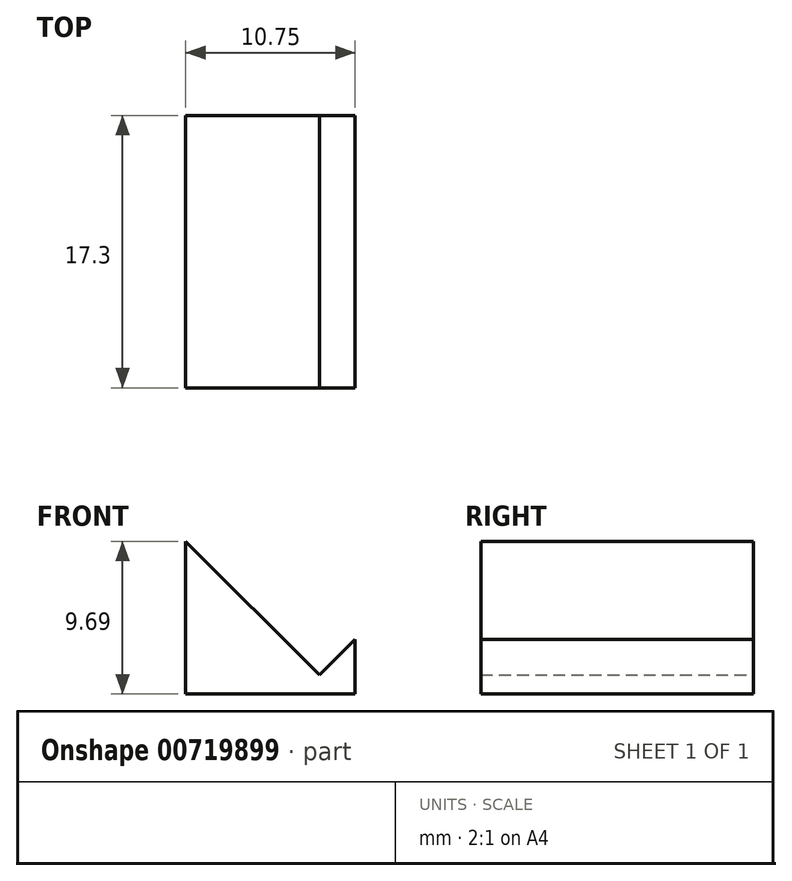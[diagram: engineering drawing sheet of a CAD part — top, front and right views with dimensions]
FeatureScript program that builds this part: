
annotation { "Feature Type Name" : "Feature", "Feature Type Description" : "" }
export const myFeature = defineFeature(function(context is Context, id is Id, definition is map)
    precondition{}
    {
        {
            var Q0;
            Q0=qCreatedBy(makeId("Front.planeOp"),FACE);
            var sketch = newSketch(context, id + "F0", { "sketchPlane" : qUnion([Q0])});
            skLineSegment(sketch, "E0", {"start": v(0, 0) * mm, "end": v(0, 1.2) * mm});
            skLineSegment(sketch, "E1", {"start": v(0, 1.2) * mm, "end": v(-8.49, 9.69) * mm});
            skLineSegment(sketch, "E2", {"start": v(-8.49, 9.69) * mm, "end": v(-8.49, 0) * mm});
            skLineSegment(sketch, "E3", {"start": v(-8.49, 0) * mm, "end": v(0, 0) * mm});
            skLineSegment(sketch, "E4", {"start": v(0, 1.2) * mm, "end": v(2.26, 3.46) * mm});
            skLineSegment(sketch, "E5", {"start": v(2.26, 3.46) * mm, "end": v(2.26, 0) * mm});
            skLineSegment(sketch, "E6", {"start": v(2.26, 0) * mm, "end": v(0, 0) * mm});
            skSolve(sketch);
        }
        {
            var Q0;
            Q0=makeQuery(id+"F0.imprint","IMPRINT",FACE,{"disambiguationData":[TD([[makeQuery(id+"F0.imprint","IMPRINT",EDGE,{"derivedFrom":sQuery(id+"F0.wireOp",EDGE,"E0")}),1.0]])]});
            var Q1;
            Q1=makeQuery(id+"F0.imprint","IMPRINT",FACE,{"disambiguationData":[TD([[makeQuery(id+"F0.imprint","IMPRINT",EDGE,{"derivedFrom":sQuery(id+"F0.wireOp",EDGE,"E0")}),-1.0]])]});
            extrude(context, id + "F1", {"entities" : qUnion([Q0, Q1]), "depth" : 17.3 * mm, "offsetDistance" : 25 * mm});
        }
    });
